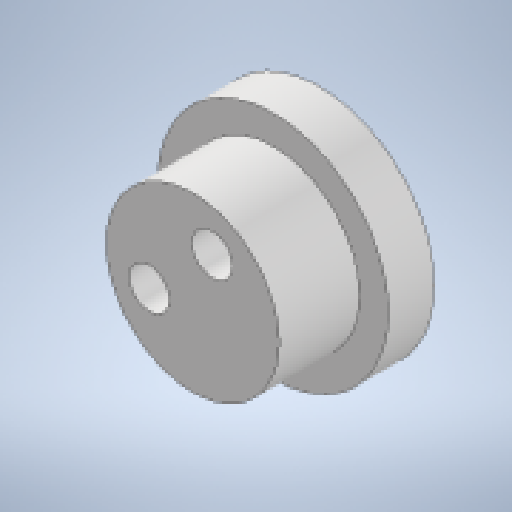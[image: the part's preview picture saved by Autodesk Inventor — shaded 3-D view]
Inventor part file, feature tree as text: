
AUTODESK INVENTOR PART (.ipt)
format: ipt  version: 2023 (Build 270158000, 158)  size: 157,184 bytes
history: native  units: in
note: dims shown in document units (in); Inventor stores cm internally (conversion verified against a paired STEP export)
features: other x3, extrude x2, sketch x2, reference x2
ambient origin geometry x8: Origin, YZ Plane, XZ Plane, XY Plane, X Axis, Y Axis, Z Axis, Center Point
bodies: Solid1 (feature_tree)
feature tree (9):
  extrude  "Extrusion1"  Depth=0.1575in TaperAngle=0.0deg
  extrude  "Extrusion2"  Depth=0.2756in TaperAngle=0.0deg
  sketch  "Sketch1"  dims[d1=0.7874in d2=0.1575in d3=0.0in]
  reference  "Reference1"
  reference  "Reference2"
  sketch  "Sketch2"  dims[d4=0.5906in d5=0.2756in d6=0.0in d7=0.0591in d8=0.315in]
  other  "<userpath>\OneDrive\Documents\Robotics Club\Cycloidal Drive\Drive.iam"
  other  "Drive.iam"
  other  "Shaft-2:1"
